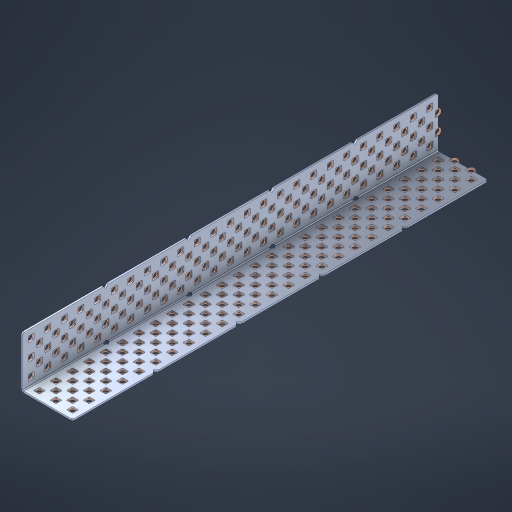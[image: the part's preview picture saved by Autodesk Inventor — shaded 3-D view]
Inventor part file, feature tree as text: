
AUTODESK INVENTOR PART (.ipt)
format: ipt  version: 2023 (Build 270158000, 158)  size: 2,580,992 bytes
history: native  units: in
note: dims shown in document units (in); Inventor stores cm internally (conversion verified against a paired STEP export)
features: other x256, extrude x248, sheet_metal_op x8, sketch x7, pattern_linear x3, mirror x1, chamfer x1
ambient origin geometry x8: Origin, YZ Plane, XZ Plane, XY Plane, X Axis, Y Axis, Z Axis, Center Point
bodies: Solid1 (feature_tree), Body (feature_tree)
feature tree (524):
  sheet_metal_op  "Flanges"
  sheet_metal_op  "Body Pattern"
  pattern_linear  "Center Double"  Spacing1=1.5in  [1 undecoded]
  pattern_linear  "Center Pattern"  Spacing1=0.1875in  [1 undecoded]
  other  "Arc Length"
  pattern_linear  "Notch Pattern"  Spacing1=0.0469in  [1 undecoded]
  other  "Diagonal Plane"
  mirror  "Everything Mirrored"
  chamfer  "End Chamfer"
  sketch  "Sketch1"  dims[d0=1.5in]
  other  "Plate1"
  sketch  "Sketch2"  dims[d1=12.5in]
  other  "Plate2"
  sheet_metal_op  "Bend1"
  sheet_metal_op  "Corner1"
  sketch  "Sketch8"  dims[d2=0.0469in]
  sketch  "Sketch9"  dims[d3=0.0469in]
  other  "Srf91"
  sheet_metal_op  "Body Pattern Sketch"
  other  "Srf92"
  sketch  "Sketch13"  dims[d4=0.0234in]
  sketch  "Sketch15"  dims[d5=0.0938in]
  sketch  "Sketch16"  dims[d6=0.0469in d7=1.5in d8=90.0deg d9=0.0312in d10=0.1875in d11=0.0469in d12=0.0469in d49=0.182in d50=0.02in d52=0.25in d53=0.0469in d54=0.0in d55=0.172in d56=1.0in d57=0.0in d85=0.1473in d86=0.1659in d89=0.0469in d90=0.0in d91=0.04in d92=0.0491in d95=2.5in d96=0.04in d97=0.25in d98=45.0deg d106=0.182in d107=0.02in d110=0.0469in d111=0.0in d112=0.172in d113=0.5in d114=0.0in d117=0.5in d126=0.0491in d127=0.1227in d128=0.08in d129=0.04in d130=2.5in d131=0.25in d132=9.8425in d134=0.5in d135=1.1811in d137=0.5in d140=0.5in d141=1.0in d142=0.3937in d144=0.5in d145=0.071in d146=0.7874in d148=0.5in]
  other  "Srf786"
  other  "Srf856"
  other  "Srf889"
  other  "Srf890"
  other  "Srf891"
  other  "Srf1275"
  other  "Srf1276"
  other  "Srf1278"
  other  "Srf1277"
  other  "Srf1285"
  other  "Srf1286"
  other  "Srf1287"
  other  "Srf1445"
  other  "Srf1446"
  other  "Srf1447"
  other  "Srf1448"
  other  "Srf1449"
  other  "Srf1537"
  other  "Srf1538"
  other  "Srf1539"
  other  "Srf1540"
  other  "Srf1541"
  other  "Srf1807"
  other  "Srf1808"
  other  "Srf1809"
  other  "Srf1810"
  other  "Srf1811"
  other  "Srf1812"
  other  "Srf1813"
  other  "Srf1814"
  other  "Srf1815"
  other  "Srf1816"
  other  "Srf1817"
  other  "Srf1818"
  other  "Srf1819"
  other  "Srf1820"
  other  "Srf1821"
  other  "Srf1822"
  other  "Srf1959"
  other  "Srf1960"
  other  "Srf1961"
  other  "Srf1962"
  other  "Srf1963"
  other  "Srf1964"
  other  "Srf1965"
  other  "Srf1966"
  other  "Srf1967"
  other  "Srf1968"
  other  "Srf1969"
  other  "Srf1970"
  other  "Srf1971"
  other  "Srf1972"
  other  "Srf1973"
  other  "Srf1974"
  other  "Srf2009"
  other  "Srf2010"
  other  "Srf2011"
  other  "Srf2012"
  other  "Srf2013"
  other  "Srf2014"
  other  "Srf2015"
  other  "Srf2016"
  other  "Srf2017"
  other  "Srf2018"
  other  "Srf2019"
  other  "Srf2020"
  other  "Srf2021"
  other  "Srf2022"
  other  "Srf2023"
  other  "Srf2024"
  other  "Srf2025"
  other  "Srf2026"
  other  "Srf2027"
  other  "Srf2028"
  other  "Srf2029"
  other  "Srf2030"
  other  "Srf2031"
  other  "Srf2032"
  other  "Srf2033"
  other  "Srf2043"
  other  "Srf2044"
  other  "Srf2045"
  other  "Srf2046"
  other  "Srf2047"
  other  "Srf2048"
  other  "Srf2049"
  other  "Srf2050"
  other  "Srf2051"
  other  "Srf2052"
  other  "Srf2053"
  other  "Srf2054"
  other  "Srf2055"
  other  "Srf2056"
  other  "Srf2057"
  other  "Srf2058"
  other  "Srf2059"
  other  "Srf2060"
  other  "Srf2061"
  other  "Srf2062"
  other  "Srf2063"
  other  "Srf2064"
  other  "Srf2065"
  other  "Srf2066"
  other  "Srf2076"
  other  "Srf2077"
  other  "Srf2078"
  other  "Srf2079"
  other  "Srf2080"
  other  "Srf2081"
  other  "Srf2082"
  other  "Srf2083"
  other  "Srf2084"
  other  "Srf2085"
  other  "Srf2086"
  other  "Srf2087"
  other  "Srf2088"
  other  "Srf2089"
  other  "Srf2090"
  other  "Srf2091"
  other  "Srf2092"
  other  "Srf2093"
  other  "Srf2094"
  other  "Srf2095"
  other  "Srf2096"
  other  "Srf2097"
  other  "Srf2098"
  other  "Srf2099"
  other  "Srf2100"
  other  "Srf2101"
  other  "Srf2102"
  other  "Srf2103"
  other  "Srf2104"
  other  "Srf2105"
  other  "Srf2106"
  other  "Srf2107"
  other  "Srf2108"
  other  "Srf2109"
  other  "Srf2110"
  other  "Srf2111"
  other  "Srf2112"
  other  "Srf2113"
  other  "Srf2114"
  other  "Srf2115"
  other  "Srf2116"
  other  "Srf2117"
  other  "Srf2118"
  other  "Srf2119"
  other  "Srf2120"
  other  "Srf2121"
  other  "Srf2122"
  other  "Srf2123"
  other  "Srf2124"
  other  "Srf2125"
  other  "Srf2126"
  other  "Srf2127"
  other  "Srf2128"
  other  "Srf2129"
  other  "Srf2130"
  other  "Srf2131"
  other  "Srf2132"
  other  "Srf2133"
  other  "Srf2134"
  other  "Srf2135"
  other  "Srf2136"
  other  "Srf2137"
  other  "Srf2138"
  other  "Srf2139"
  other  "Srf2140"
  other  "Srf2141"
  other  "Srf2142"
  other  "Srf2143"
  other  "Srf2144"
  other  "Srf2145"
  other  "Srf2146"
  other  "Srf2147"
  other  "Srf2148"
  other  "Srf2179"
  other  "Srf2180"
  other  "Srf2181"
  other  "Srf2182"
  other  "Srf2183"
  other  "Srf2184"
  other  "Srf2185"
  other  "Srf2186"
  other  "Srf2187"
  other  "Srf2188"
  other  "Srf2189"
  other  "Srf2190"
  other  "Srf2191"
  other  "Srf2192"
  other  "Srf2193"
  other  "Srf2194"
  other  "Srf2195"
  other  "Srf2196"
  other  "Srf2197"
  other  "Srf2198"
  other  "Srf2199"
  other  "Srf2200"
  other  "Srf2201"
  other  "Srf2202"
  other  "Srf2203"
  other  "Srf2204"
  other  "Srf2205"
  other  "Srf2206"
  other  "Srf2207"
  other  "Srf2208"
  other  "Srf2209"
  other  "Srf2210"
  other  "Srf2211"
  other  "Srf2212"
  other  "Srf2213"
  other  "Srf2214"
  other  "Srf2215"
  other  "Srf2216"
  other  "Srf2217"
  other  "Srf2218"
  other  "Srf2219"
  other  "Srf2220"
  other  "Srf2221"
  other  "Srf2222"
  other  "Srf2223"
  other  "Srf2224"
  other  "Srf2225"
  other  "Srf2226"
  other  "Srf2227"
  other  "Srf2228"
  other  "Srf2229"
  other  "Srf2230"
  other  "Srf2231"
  other  "Srf2232"
  other  "Srf2233"
  other  "Srf2234"
  other  "Srf2235"
  other  "Srf2236"
  other  "Srf2237"
  other  "Srf2238"
  other  "Srf2239"
  other  "Srf2240"
  other  "Srf2241"
  other  "Srf2242"
  other  "Srf2243"
  other  "Srf2244"
  other  "Srf2245"
  other  "Srf2246"
  other  "Srf2247"
  other  "Srf2248"
  other  "Srf2249"
  other  "Srf2250"
  sheet_metal_op  "Body Stamp"
  sheet_metal_op  "Body Circle"
  other  "Center Stamp"
  other  "Center Circle"
  sheet_metal_op  "Notch"
  extrude  "ExtrusionSrf92"  Depth=0.0469in
  extrude  "ExtrusionSrf856"  Depth=0.182in
  extrude  "ExtrusionSrf889"  Depth=0.02in
  extrude  "ExtrusionSrf890"  Depth=0.25in
  extrude  "ExtrusionSrf891"  Depth=0.0469in
  extrude  "ExtrusionSrf1275"  TaperAngle=0.0deg  [1 undecoded]
  extrude  "ExtrusionSrf1276"  Depth=0.5in
  extrude  "ExtrusionSrf1277"  Depth=1.0in TaperAngle=0.0deg
  extrude  "ExtrusionSrf1345"  Depth=0.5in
  extrude  "ExtrusionSrf1346"  Depth=0.5in
  extrude  "ExtrusionSrf1347"  Depth=0.0469in
  extrude  "ExtrusionSrf1348"  Depth=0.5in TaperAngle=0.0deg
  extrude  "ExtrusionSrf1445"  Depth=0.5in
  extrude  "ExtrusionSrf1446"  Depth=0.25in TaperAngle=45.0deg
  extrude  "ExtrusionSrf1447"  Depth=0.182in
  extrude  "ExtrusionSrf1448"  Depth=0.02in
  extrude  "ExtrusionSrf1449"  Depth=0.0469in
  extrude  "ExtrusionSrf1537"  TaperAngle=0.0deg  [1 undecoded]
  extrude  "ExtrusionSrf1538"  Depth=0.5in
  extrude  "ExtrusionSrf1539"  Depth=0.5in TaperAngle=0.0deg
  extrude  "ExtrusionSrf1540"  Depth=0.5in
  extrude  "ExtrusionSrf1541"  Depth=0.5in
  extrude  "ExtrusionSrf1807"  Depth=0.5in
  extrude  "ExtrusionSrf1808"  Depth=0.5in
  extrude  "ExtrusionSrf1809"  Depth=0.5in
  extrude  "ExtrusionSrf1810"  Depth=0.5in
  extrude  "ExtrusionSrf1811"  Depth=0.25in
  extrude  "ExtrusionSrf1812"  Depth=0.5in
  extrude  "ExtrusionSrf1813"  Depth=0.5in
  extrude  "ExtrusionSrf1814"  Depth=0.5in
  extrude  "ExtrusionSrf1815"  Depth=1.0in
  extrude  "ExtrusionSrf1816"  Depth=0.3937in
  extrude  "ExtrusionSrf1817"  Depth=0.5in
  extrude  "ExtrusionSrf1818"  Depth=0.5in
  extrude  "ExtrusionSrf1819"  [1 undecoded]
  extrude  "ExtrusionSrf1820"  [1 undecoded]
  extrude  "ExtrusionSrf1821"  [1 undecoded]
  extrude  "ExtrusionSrf1822"  [1 undecoded]
  extrude  "ExtrusionSrf1959"  [1 undecoded]
  extrude  "ExtrusionSrf1960"  [1 undecoded]
  extrude  "ExtrusionSrf1961"  [1 undecoded]
  extrude  "ExtrusionSrf1962"  [1 undecoded]
  extrude  "ExtrusionSrf1963"  [1 undecoded]
  extrude  "ExtrusionSrf1964"  [1 undecoded]
  extrude  "ExtrusionSrf1965"  [1 undecoded]
  extrude  "ExtrusionSrf1966"  [1 undecoded]
  extrude  "ExtrusionSrf1967"  [1 undecoded]
  extrude  "ExtrusionSrf1968"  [1 undecoded]
  extrude  "ExtrusionSrf1969"  [1 undecoded]
  extrude  "ExtrusionSrf1970"  [1 undecoded]
  extrude  "ExtrusionSrf1971"  [1 undecoded]
  extrude  "ExtrusionSrf1972"  [1 undecoded]
  extrude  "ExtrusionSrf1973"  [1 undecoded]
  extrude  "ExtrusionSrf1974"  [1 undecoded]
  extrude  "ExtrusionSrf2009"  [1 undecoded]
  extrude  "ExtrusionSrf2010"  [1 undecoded]
  extrude  "ExtrusionSrf2011"  [1 undecoded]
  extrude  "ExtrusionSrf2012"  [1 undecoded]
  extrude  "ExtrusionSrf2013"  [1 undecoded]
  extrude  "ExtrusionSrf2014"  [1 undecoded]
  extrude  "ExtrusionSrf2015"  [1 undecoded]
  extrude  "ExtrusionSrf2016"  [1 undecoded]
  extrude  "ExtrusionSrf2017"  [1 undecoded]
  extrude  "ExtrusionSrf2018"  [1 undecoded]
  extrude  "ExtrusionSrf2019"  [1 undecoded]
  extrude  "ExtrusionSrf2020"  [1 undecoded]
  extrude  "ExtrusionSrf2021"  [1 undecoded]
  extrude  "ExtrusionSrf2022"  [1 undecoded]
  extrude  "ExtrusionSrf2023"  [1 undecoded]
  extrude  "ExtrusionSrf2024"  [1 undecoded]
  extrude  "ExtrusionSrf2025"  [1 undecoded]
  extrude  "ExtrusionSrf2026"  [1 undecoded]
  extrude  "ExtrusionSrf2027"  [1 undecoded]
  extrude  "ExtrusionSrf2028"  [1 undecoded]
  extrude  "ExtrusionSrf2029"  [1 undecoded]
  extrude  "ExtrusionSrf2030"  [1 undecoded]
  extrude  "ExtrusionSrf2031"  [1 undecoded]
  extrude  "ExtrusionSrf2032"  [1 undecoded]
  extrude  "ExtrusionSrf2033"  [1 undecoded]
  extrude  "ExtrusionSrf2043"  [1 undecoded]
  extrude  "ExtrusionSrf2044"  [1 undecoded]
  extrude  "ExtrusionSrf2045"  [1 undecoded]
  extrude  "ExtrusionSrf2046"  [1 undecoded]
  extrude  "ExtrusionSrf2047"  [1 undecoded]
  extrude  "ExtrusionSrf2048"  [1 undecoded]
  extrude  "ExtrusionSrf2049"  [1 undecoded]
  extrude  "ExtrusionSrf2050"  [1 undecoded]
  extrude  "ExtrusionSrf2051"  [1 undecoded]
  extrude  "ExtrusionSrf2052"  [1 undecoded]
  extrude  "ExtrusionSrf2053"  [1 undecoded]
  extrude  "ExtrusionSrf2054"  [1 undecoded]
  extrude  "ExtrusionSrf2055"  [1 undecoded]
  extrude  "ExtrusionSrf2056"  [1 undecoded]
  extrude  "ExtrusionSrf2057"  [1 undecoded]
  extrude  "ExtrusionSrf2058"  [1 undecoded]
  extrude  "ExtrusionSrf2059"  [1 undecoded]
  extrude  "ExtrusionSrf2060"  [1 undecoded]
  extrude  "ExtrusionSrf2061"  [1 undecoded]
  extrude  "ExtrusionSrf2062"  [1 undecoded]
  extrude  "ExtrusionSrf2063"  [1 undecoded]
  extrude  "ExtrusionSrf2064"  [1 undecoded]
  extrude  "ExtrusionSrf2065"  [1 undecoded]
  extrude  "ExtrusionSrf2066"  [1 undecoded]
  extrude  "ExtrusionSrf2076"  [1 undecoded]
  extrude  "ExtrusionSrf2077"  [1 undecoded]
  extrude  "ExtrusionSrf2078"  [1 undecoded]
  extrude  "ExtrusionSrf2079"  [1 undecoded]
  extrude  "ExtrusionSrf2080"  [1 undecoded]
  extrude  "ExtrusionSrf2081"  [1 undecoded]
  extrude  "ExtrusionSrf2082"  [1 undecoded]
  extrude  "ExtrusionSrf2083"  [1 undecoded]
  extrude  "ExtrusionSrf2084"  [1 undecoded]
  extrude  "ExtrusionSrf2085"  [1 undecoded]
  extrude  "ExtrusionSrf2086"  [1 undecoded]
  extrude  "ExtrusionSrf2087"  [1 undecoded]
  extrude  "ExtrusionSrf2088"  [1 undecoded]
  extrude  "ExtrusionSrf2089"  [1 undecoded]
  extrude  "ExtrusionSrf2090"  [1 undecoded]
  extrude  "ExtrusionSrf2091"  [1 undecoded]
  extrude  "ExtrusionSrf2092"  [1 undecoded]
  extrude  "ExtrusionSrf2093"  [1 undecoded]
  extrude  "ExtrusionSrf2094"  [1 undecoded]
  extrude  "ExtrusionSrf2095"  [1 undecoded]
  extrude  "ExtrusionSrf2096"  [1 undecoded]
  extrude  "ExtrusionSrf2097"  [1 undecoded]
  extrude  "ExtrusionSrf2098"  [1 undecoded]
  extrude  "ExtrusionSrf2099"  [1 undecoded]
  extrude  "ExtrusionSrf2100"  [1 undecoded]
  extrude  "ExtrusionSrf2101"  [1 undecoded]
  extrude  "ExtrusionSrf2102"  [1 undecoded]
  extrude  "ExtrusionSrf2103"  [1 undecoded]
  extrude  "ExtrusionSrf2104"  [1 undecoded]
  extrude  "ExtrusionSrf2105"  [1 undecoded]
  extrude  "ExtrusionSrf2106"  [1 undecoded]
  extrude  "ExtrusionSrf2107"  [1 undecoded]
  extrude  "ExtrusionSrf2108"  [1 undecoded]
  extrude  "ExtrusionSrf2109"  [1 undecoded]
  extrude  "ExtrusionSrf2110"  [1 undecoded]
  extrude  "ExtrusionSrf2111"  [1 undecoded]
  extrude  "ExtrusionSrf2112"  [1 undecoded]
  extrude  "ExtrusionSrf2113"  [1 undecoded]
  extrude  "ExtrusionSrf2114"  [1 undecoded]
  extrude  "ExtrusionSrf2115"  [1 undecoded]
  extrude  "ExtrusionSrf2116"  [1 undecoded]
  extrude  "ExtrusionSrf2117"  [1 undecoded]
  extrude  "ExtrusionSrf2118"  [1 undecoded]
  extrude  "ExtrusionSrf2119"  [1 undecoded]
  extrude  "ExtrusionSrf2120"  [1 undecoded]
  extrude  "ExtrusionSrf2121"  [1 undecoded]
  extrude  "ExtrusionSrf2122"  [1 undecoded]
  extrude  "ExtrusionSrf2123"  [1 undecoded]
  extrude  "ExtrusionSrf2124"  [1 undecoded]
  extrude  "ExtrusionSrf2125"  [1 undecoded]
  extrude  "ExtrusionSrf2126"  [1 undecoded]
  extrude  "ExtrusionSrf2127"  [1 undecoded]
  extrude  "ExtrusionSrf2128"  [1 undecoded]
  extrude  "ExtrusionSrf2129"  [1 undecoded]
  extrude  "ExtrusionSrf2130"  [1 undecoded]
  extrude  "ExtrusionSrf2131"  [1 undecoded]
  extrude  "ExtrusionSrf2132"  [1 undecoded]
  extrude  "ExtrusionSrf2133"  [1 undecoded]
  extrude  "ExtrusionSrf2134"  [1 undecoded]
  extrude  "ExtrusionSrf2135"  [1 undecoded]
  extrude  "ExtrusionSrf2136"  [1 undecoded]
  extrude  "ExtrusionSrf2137"  [1 undecoded]
  extrude  "ExtrusionSrf2138"  [1 undecoded]
  extrude  "ExtrusionSrf2139"  [1 undecoded]
  extrude  "ExtrusionSrf2140"  [1 undecoded]
  extrude  "ExtrusionSrf2141"  [1 undecoded]
  extrude  "ExtrusionSrf2142"  [1 undecoded]
  extrude  "ExtrusionSrf2143"  [1 undecoded]
  extrude  "ExtrusionSrf2144"  [1 undecoded]
  extrude  "ExtrusionSrf2145"  [1 undecoded]
  extrude  "ExtrusionSrf2146"  [1 undecoded]
  extrude  "ExtrusionSrf2147"  [1 undecoded]
  extrude  "ExtrusionSrf2148"  [1 undecoded]
  extrude  "ExtrusionSrf2179"  [1 undecoded]
  extrude  "ExtrusionSrf2180"  [1 undecoded]
  extrude  "ExtrusionSrf2181"  [1 undecoded]
  extrude  "ExtrusionSrf2182"  [1 undecoded]
  extrude  "ExtrusionSrf2183"  [1 undecoded]
  extrude  "ExtrusionSrf2184"  [1 undecoded]
  extrude  "ExtrusionSrf2185"  [1 undecoded]
  extrude  "ExtrusionSrf2186"  [1 undecoded]
  extrude  "ExtrusionSrf2187"  [1 undecoded]
  extrude  "ExtrusionSrf2188"  [1 undecoded]
  extrude  "ExtrusionSrf2189"  [1 undecoded]
  extrude  "ExtrusionSrf2190"  [1 undecoded]
  extrude  "ExtrusionSrf2191"  [1 undecoded]
  extrude  "ExtrusionSrf2192"  [1 undecoded]
  extrude  "ExtrusionSrf2193"  [1 undecoded]
  extrude  "ExtrusionSrf2194"  [1 undecoded]
  extrude  "ExtrusionSrf2195"  [1 undecoded]
  extrude  "ExtrusionSrf2196"  [1 undecoded]
  extrude  "ExtrusionSrf2197"  [1 undecoded]
  extrude  "ExtrusionSrf2198"  [1 undecoded]
  extrude  "ExtrusionSrf2199"  [1 undecoded]
  extrude  "ExtrusionSrf2200"  [1 undecoded]
  extrude  "ExtrusionSrf2201"  [1 undecoded]
  extrude  "ExtrusionSrf2202"  [1 undecoded]
  extrude  "ExtrusionSrf2203"  [1 undecoded]
  extrude  "ExtrusionSrf2204"  [1 undecoded]
  extrude  "ExtrusionSrf2205"  [1 undecoded]
  extrude  "ExtrusionSrf2206"  [1 undecoded]
  extrude  "ExtrusionSrf2207"  [1 undecoded]
  extrude  "ExtrusionSrf2208"  [1 undecoded]
  extrude  "ExtrusionSrf2209"  [1 undecoded]
  extrude  "ExtrusionSrf2210"  [1 undecoded]
  extrude  "ExtrusionSrf2211"  [1 undecoded]
  extrude  "ExtrusionSrf2212"  [1 undecoded]
  extrude  "ExtrusionSrf2213"  [1 undecoded]
  extrude  "ExtrusionSrf2214"  [1 undecoded]
  extrude  "ExtrusionSrf2215"  [1 undecoded]
  extrude  "ExtrusionSrf2216"  [1 undecoded]
  extrude  "ExtrusionSrf2217"  [1 undecoded]
  extrude  "ExtrusionSrf2218"  [1 undecoded]
  extrude  "ExtrusionSrf2219"  [1 undecoded]
  extrude  "ExtrusionSrf2220"  [1 undecoded]
  extrude  "ExtrusionSrf2221"  [1 undecoded]
  extrude  "ExtrusionSrf2222"  [1 undecoded]
  extrude  "ExtrusionSrf2223"  [1 undecoded]
  extrude  "ExtrusionSrf2224"  [1 undecoded]
  extrude  "ExtrusionSrf2225"  [1 undecoded]
  extrude  "ExtrusionSrf2226"  [1 undecoded]
  extrude  "ExtrusionSrf2227"  [1 undecoded]
  extrude  "ExtrusionSrf2228"  [1 undecoded]
  extrude  "ExtrusionSrf2229"  [1 undecoded]
  extrude  "ExtrusionSrf2230"  [1 undecoded]
  extrude  "ExtrusionSrf2231"  [1 undecoded]
  extrude  "ExtrusionSrf2232"  [1 undecoded]
  extrude  "ExtrusionSrf2233"  [1 undecoded]
  extrude  "ExtrusionSrf2234"  [1 undecoded]
  extrude  "ExtrusionSrf2235"  [1 undecoded]
  extrude  "ExtrusionSrf2236"  [1 undecoded]
  extrude  "ExtrusionSrf2237"  [1 undecoded]
  extrude  "ExtrusionSrf2238"  [1 undecoded]
  extrude  "ExtrusionSrf2239"  [1 undecoded]
  extrude  "ExtrusionSrf2240"  [1 undecoded]
  extrude  "ExtrusionSrf2241"  [1 undecoded]
  extrude  "ExtrusionSrf2242"  [1 undecoded]
  extrude  "ExtrusionSrf2243"  [1 undecoded]
  extrude  "ExtrusionSrf2244"  [1 undecoded]
  extrude  "ExtrusionSrf2245"  [1 undecoded]
  extrude  "ExtrusionSrf2246"  [1 undecoded]
  extrude  "ExtrusionSrf2247"  [1 undecoded]
  extrude  "ExtrusionSrf2248"  [1 undecoded]
  extrude  "ExtrusionSrf2249"  [1 undecoded]
  extrude  "ExtrusionSrf2250"  [1 undecoded]
note: 219 required parameter values undecoded (feature->parameter linkage not recoverable at this tier; creation-order binding heuristic only, values carry confidence <= 0.55)
